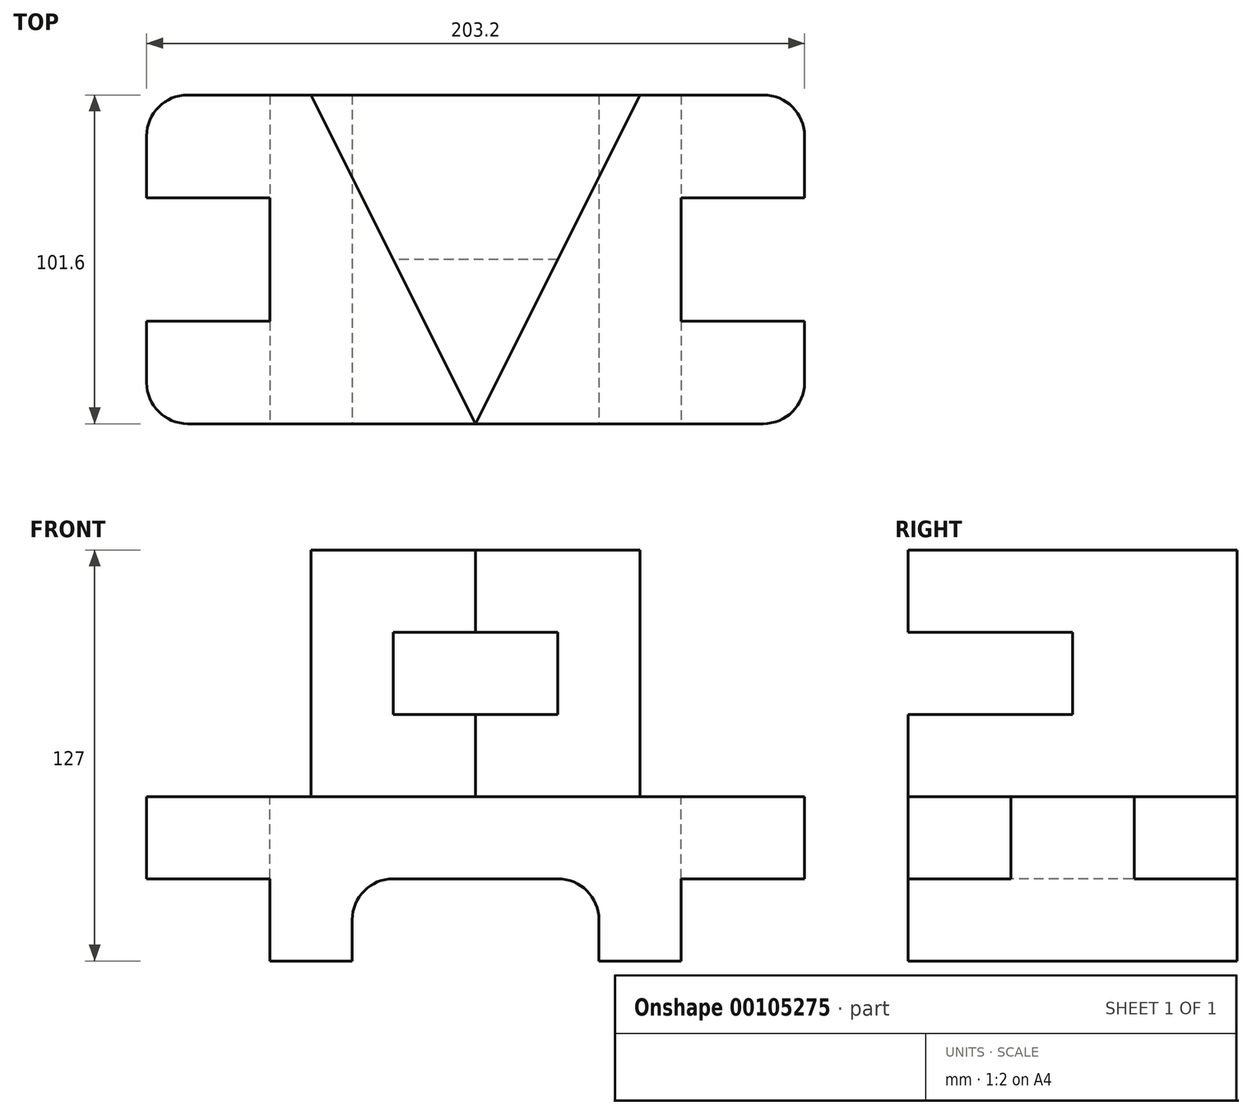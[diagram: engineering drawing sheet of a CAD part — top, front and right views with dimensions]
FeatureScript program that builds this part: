
annotation { "Feature Type Name" : "Feature", "Feature Type Description" : "" }
export const myFeature = defineFeature(function(context is Context, id is Id, definition is map)
    precondition{}
    {
        {
            var Q0;
            Q0=qCreatedBy(makeId("Front.planeOp"),FACE);
            var sketch = newSketch(context, id + "F0", { "sketchPlane" : qUnion([Q0])});
            skLineSegment(sketch, "E0.bottom", {"start": v(38.1, 0) * mm, "end": v(63.5, 0) * mm});
            skLineSegment(sketch, "E0.top", {"start": v(0, 127) * mm, "end": v(203.2, 127) * mm});
            skLineSegment(sketch, "E0.left", {"start": v(0, 25.4) * mm, "end": v(0, 127) * mm});
            skLineSegment(sketch, "E0.right", {"start": v(203.2, 25.4) * mm, "end": v(203.2, 127) * mm});
            skLineSegment(sketch, "E1.top", {"start": v(203.2, 25.4) * mm, "end": v(165.1, 25.4) * mm});
            skLineSegment(sketch, "E1.right", {"start": v(165.1, 0) * mm, "end": v(165.1, 25.4) * mm});
            skLineSegment(sketch, "E2.top", {"start": v(0, 25.4) * mm, "end": v(38.1, 25.4) * mm});
            skLineSegment(sketch, "E2.right", {"start": v(38.1, 0) * mm, "end": v(38.1, 25.4) * mm});
            skPoint(sketch, "E3.orphan", {"position": v(0, 0) * mm});
            skLineSegment(sketch, "E4", {"start": v(63.5, 0) * mm, "end": v(63.5, 12.7) * mm});
            skLineSegment(sketch, "E5", {"start": v(76.2, 25.4) * mm, "end": v(127, 25.4) * mm});
            skLineSegment(sketch, "E6", {"start": v(139.7, 12.7) * mm, "end": v(139.7, 0) * mm});
            skLineSegment(sketch, "E7.trimOffspring", {"start": v(139.7, 0) * mm, "end": v(165.1, 0) * mm});
            skArc(sketch, "E8", {"start": v(63.5, 12.7) * mm, "mid": v(67.22, 21.68) * mm, "end": v(76.2, 25.4) * mm});
            skPoint(sketch, "E8.centerSnap0", {"position": v(63.5, 12.7) * mm});
            skPoint(sketch, "E9.orphan", {"position": v(63.5, 25.4) * mm});
            skPoint(sketch, "E10.visualSharp", {"position": v(139.7, 25.4) * mm});
            skArc(sketch, "E10.filletArc", {"start": v(139.7, 12.7) * mm, "mid": v(135.98, 21.68) * mm, "end": v(127, 25.4) * mm});
            skSolve(sketch);
        }
        {
            var Q0;
            Q0 = qSketchRegion(id + "F0", true);
            extrude(context, id + "F1", {"entities" : qUnion([Q0]), "oppositeDirection" : true, "depth" : 101.6 * mm});
        }
        {
            var Q0;
            Q0=makeQuery(id+"F1.opExtrude","SWEPT_FACE",FACE,{"disambiguationData":[OSD([sQuery(id+"F0.wireOp",EDGE,"E0.top")])]});
            var sketch = newSketch(context, id + "F2", { "sketchPlane" : qUnion([Q0])});
            skLineSegment(sketch, "E11", {"start": v(101.6, 0) * mm, "end": v(152.4, 101.6) * mm});
            skLineSegment(sketch, "E12", {"start": v(152.4, 101.6) * mm, "end": v(50.8, 101.6) * mm});
            skLineSegment(sketch, "E13", {"start": v(50.8, 101.6) * mm, "end": v(101.6, 0) * mm});
            skLineSegment(sketch, "E14", {"start": v(152.4, 101.6) * mm, "end": v(203.2, 101.6) * mm});
            skLineSegment(sketch, "E15", {"start": v(203.2, 101.6) * mm, "end": v(203.2, 0) * mm});
            skLineSegment(sketch, "E16", {"start": v(203.2, 0) * mm, "end": v(101.6, 0) * mm});
            skLineSegment(sketch, "E17", {"start": v(0, 0) * mm, "end": v(0, 101.6) * mm});
            skLineSegment(sketch, "E18", {"start": v(0, 101.6) * mm, "end": v(50.8, 101.6) * mm});
            skSolve(sketch);
        }
        {
            var Q0;
            Q0=makeQuery(id+"F2.imprint","IMPRINT",FACE,{"disambiguationData":[TD([[makeQuery(id+"F2.imprint","IMPRINT",EDGE,{"derivedFrom":sQuery(id+"F2.wireOp",EDGE,"E11")}),-1.0]])]});
            var Q1;
            {var subQ0=sQuery(id+"F2.wireOp",EDGE,"E13");Q1=makeQuery(id+"F2.imprint","IMPRINT",FACE,{"disambiguationData":[TD([[makeQuery(id+"F2.imprint","IMPRINT",EDGE,{"derivedFrom":subQ0}),-1.0]])]});}
            extrude(context, id + "F3", {"entities" : qUnion([Q0, Q1]), "operationType" : NewBodyOperationType.REMOVE, "oppositeDirection" : true, "depth" : 76.2 * mm});
        }
        {
            var Q0;
            Q0=makeQuery(id+"F1.opExtrude","CAP_EDGE",EDGE,{"disambiguationData":[OSD([sQuery(id+"F0.wireOp",EDGE,"E0.right")])],"isStart":true});
            var Q1;
            Q1=makeQuery(id+"F1.opExtrude","CAP_EDGE",EDGE,{"disambiguationData":[OSD([sQuery(id+"F0.wireOp",EDGE,"E0.right")])],"isStart":false});
            var Q2;
            Q2=makeQuery(id+"F1.opExtrude","CAP_EDGE",EDGE,{"disambiguationData":[OSD([sQuery(id+"F0.wireOp",EDGE,"E0.left")])],"isStart":false});
            var Q3;
            Q3=makeQuery(id+"F1.opExtrude","CAP_EDGE",EDGE,{"disambiguationData":[OSD([sQuery(id+"F0.wireOp",EDGE,"E0.left")])],"isStart":true});
            fillet(context, id + "F4", {"entities" : qUnion([Q0, Q1, Q2, Q3]), "radius" : 12.7 * mm, "tangentPropagation" : true, "allowEdgeOverflow" : false});
        }
        {
            var Q0;
            Q0=makeQuery(id+"F3.boolean.opBoolean","COPY",FACE,{"derivedFrom":makeQuery(id+"F3.opExtrude","CAP_FACE",FACE,{"disambiguationData":[OSD([sQuery(id+"F0.wireOp",EDGE,"E0.top"),sQuery(id+"F2.wireOp",EDGE,"E13"),sQuery(id+"F2.wireOp",EDGE,"E17"),sQuery(id+"F2.wireOp",EDGE,"E18")])],"isStart":false})});
            var sketch = newSketch(context, id + "F5", { "sketchPlane" : qUnion([Q0])});
            skLineSegment(sketch, "E19.bottom", {"start": v(0, 69.85) * mm, "end": v(38.1, 69.85) * mm});
            skLineSegment(sketch, "E19.top", {"start": v(0, 31.75) * mm, "end": v(38.1, 31.75) * mm});
            skLineSegment(sketch, "E19.left", {"start": v(0, 69.85) * mm, "end": v(0, 31.75) * mm});
            skLineSegment(sketch, "E19.right", {"start": v(38.1, 69.85) * mm, "end": v(38.1, 31.75) * mm});
            skSolve(sketch);
        }
        {
            var Q0;
            Q0=makeQuery(id+"F5.imprint","IMPRINT",FACE,{"disambiguationData":[TD([[makeQuery(id+"F5.imprint","IMPRINT",EDGE,{"derivedFrom":sQuery(id+"F5.wireOp",EDGE,"E19.bottom")}),-1.0]])]});
            extrude(context, id + "F6", {"entities" : qUnion([Q0]), "operationType" : NewBodyOperationType.REMOVE, "endBound" : BoundingType.THROUGH_ALL, "oppositeDirection" : true, "depth" : 25.4 * mm});
        }
        {
            var Q0;
            Q0=makeQuery(id+"F3.boolean.opBoolean","COPY",FACE,{"derivedFrom":makeQuery(id+"F3.opExtrude","CAP_FACE",FACE,{"disambiguationData":[OSD([sQuery(id+"F2.wireOp",EDGE,"E11"),sQuery(id+"F2.wireOp",EDGE,"E14"),sQuery(id+"F2.wireOp",EDGE,"E15"),sQuery(id+"F2.wireOp",EDGE,"E16")])],"isStart":false})});
            var sketch = newSketch(context, id + "F7", { "sketchPlane" : qUnion([Q0])});
            skLineSegment(sketch, "E20", {"start": v(203.2, 69.85) * mm, "end": v(165.1, 69.85) * mm});
            skLineSegment(sketch, "E21", {"start": v(165.1, 69.85) * mm, "end": v(165.1, 31.75) * mm});
            skLineSegment(sketch, "E22", {"start": v(165.1, 31.75) * mm, "end": v(203.2, 31.75) * mm});
            skSolve(sketch);
        }
        {
            var Q0;
            Q0 = qSketchRegion(id + "F7", true);
            var Q1;
            {var subQ0=sQuery(id+"F7.wireOp",EDGE,"E20");Q1=makeQuery(id+"F7.imprint","IMPRINT",FACE,{"disambiguationData":[TD([[makeQuery(id+"F7.imprint","IMPRINT",EDGE,{"derivedFrom":subQ0}),1.0]])]});}
            extrude(context, id + "F8", {"entities" : qUnion([Q0, Q1]), "operationType" : NewBodyOperationType.REMOVE, "endBound" : BoundingType.THROUGH_ALL, "oppositeDirection" : true, "depth" : 25.4 * mm});
        }
        {
            var Q0;
            Q0=qCreatedBy(makeId("Right.planeOp"),FACE);
            var sketch = newSketch(context, id + "F9", { "sketchPlane" : qUnion([Q0])});
            skLineSegment(sketch, "E23", {"start": v(0, 101.6) * mm, "end": v(50.8, 101.6) * mm});
            skLineSegment(sketch, "E24", {"start": v(50.8, 101.6) * mm, "end": v(50.8, 76.2) * mm});
            skLineSegment(sketch, "E25", {"start": v(50.8, 76.2) * mm, "end": v(0, 76.2) * mm});
            skLineSegment(sketch, "E26", {"start": v(0, 76.2) * mm, "end": v(0, 101.6) * mm});
            skSolve(sketch);
        }
        {
            var Q0;
            Q0 = qSketchRegion(id + "F9", true);
            extrude(context, id + "F10", {"entities" : qUnion([Q0]), "operationType" : NewBodyOperationType.REMOVE, "endBound" : BoundingType.THROUGH_ALL, "depth" : 25.4 * mm});
        }
    });
